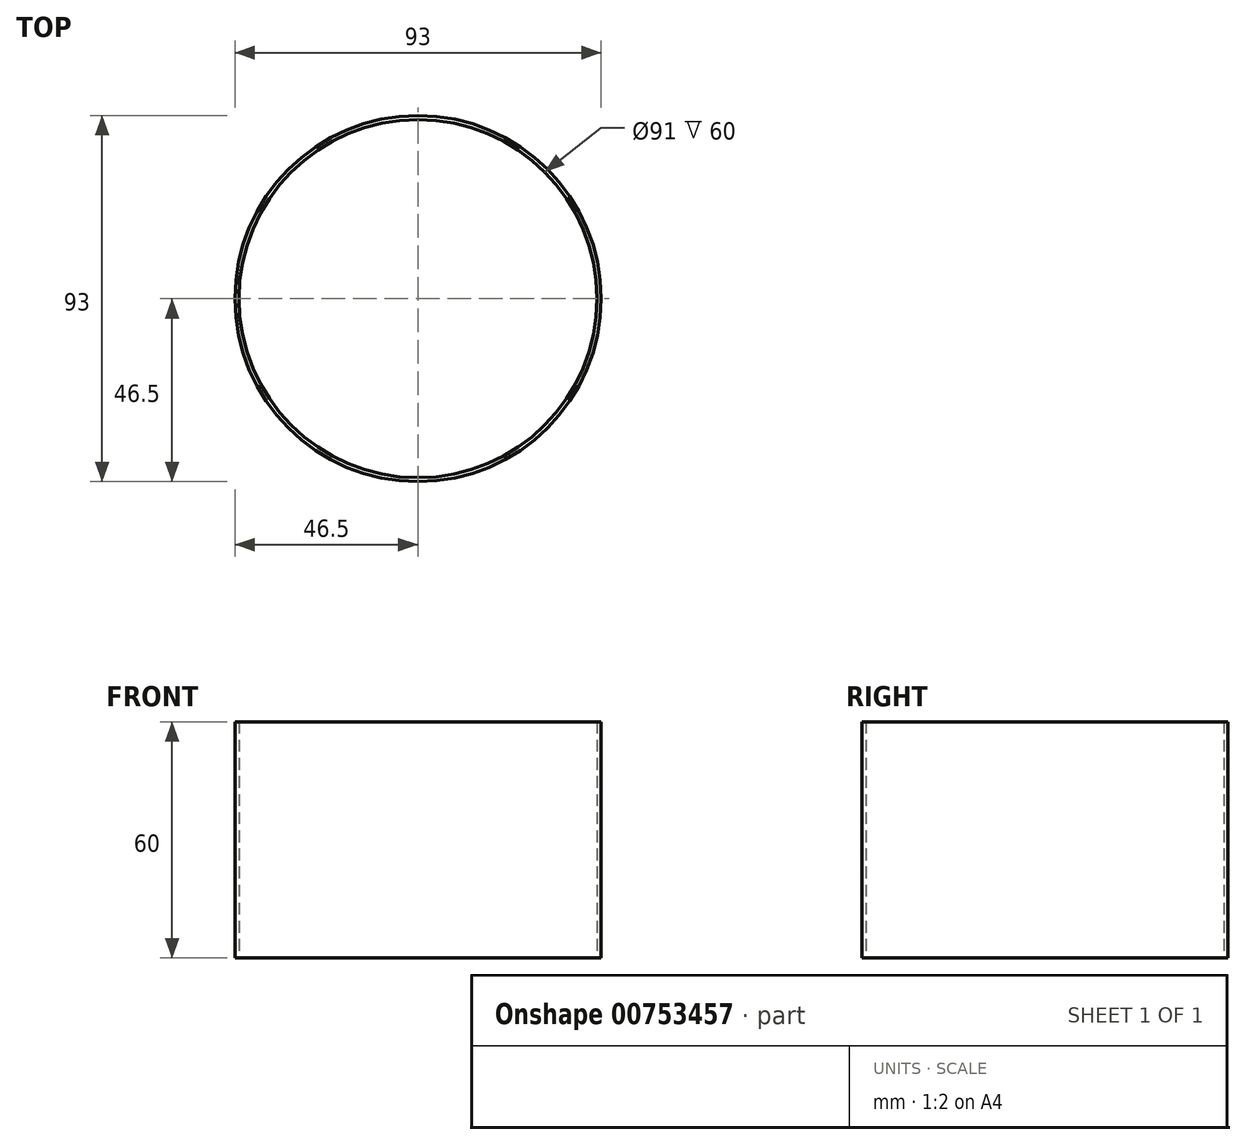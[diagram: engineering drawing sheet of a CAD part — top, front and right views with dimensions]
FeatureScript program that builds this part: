
annotation { "Feature Type Name" : "Feature", "Feature Type Description" : "" }
export const myFeature = defineFeature(function(context is Context, id is Id, definition is map)
    precondition{}
    {
        {
            var Q0;
            Q0=qCreatedBy(makeId("Top.planeOp"),FACE);
            var sketch = newSketch(context, id + "F0", { "sketchPlane" : qUnion([Q0])});
            skCircle(sketch, "E0", {"center": v(0, 0) * mm, "radius": 1155.7 * mm});
            skCircle(sketch, "E1", {"center": v(0, 0) * mm, "radius": 1380.1 * mm});
            skCircle(sketch, "E2", {"center": v(0, 0) * mm, "radius": 46.5 * mm});
            skCircle(sketch, "E3", {"center": v(0, 0) * mm, "radius": 45.5 * mm});
            skSolve(sketch);
        }
        {
            var Q0;
            Q0=makeQuery(id+"F0.imprint","IMPRINT",FACE,{"disambiguationData":[TD([[makeQuery(id+"F0.imprint","IMPRINT",EDGE,{"derivedFrom":sQuery(id+"F0.wireOp",EDGE,"E2")}),1.0]])]});
            extrude(context, id + "F1", {"entities" : qUnion([Q0]), "depth" : 60 * mm, "offsetDistance" : 25 * mm});
        }
    });
